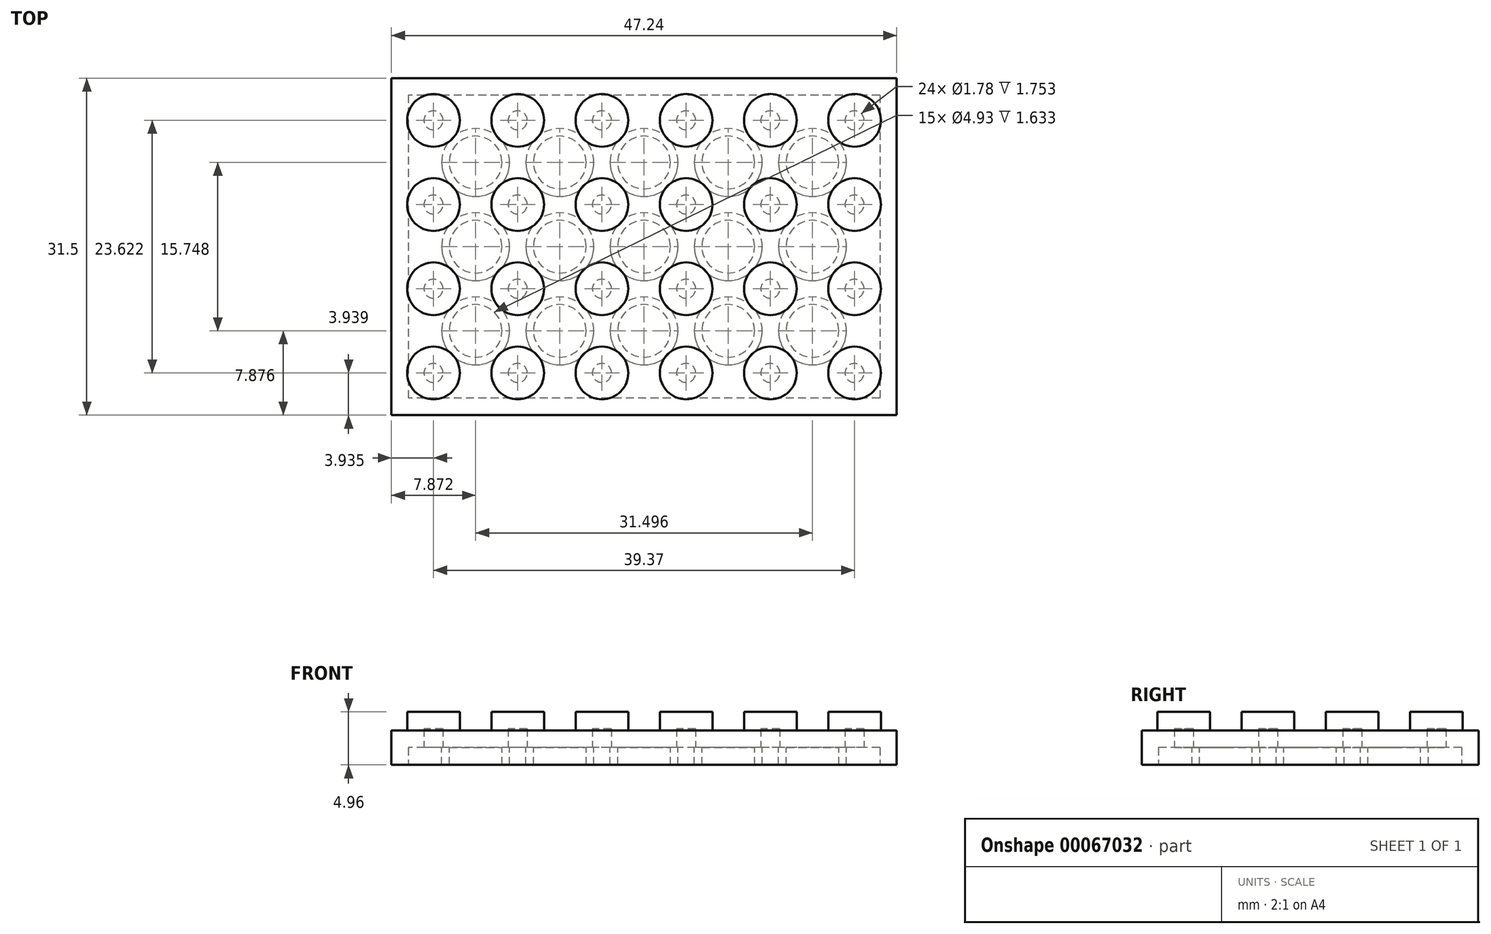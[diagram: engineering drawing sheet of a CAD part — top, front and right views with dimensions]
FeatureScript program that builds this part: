
annotation { "Feature Type Name" : "Feature", "Feature Type Description" : "" }
export const myFeature = defineFeature(function(context is Context, id is Id, definition is map)
    precondition{}
    {
        {
            var Q0;
            Q0=qCreatedBy(makeId("Top.planeOp"),FACE);
            var sketch = newSketch(context, id + "F0", { "sketchPlane" : qUnion([Q0])});
            skLineSegment(sketch, "E0.rect.bottom", {"start": v(23.62, 15.75) * mm, "end": v(-23.62, 15.75) * mm});
            skLineSegment(sketch, "E0.rect.top", {"start": v(23.62, -15.75) * mm, "end": v(-23.62, -15.75) * mm});
            skLineSegment(sketch, "E0.rect.left", {"start": v(23.62, 15.75) * mm, "end": v(23.62, -15.75) * mm});
            skLineSegment(sketch, "E0.rect.right", {"start": v(-23.62, 15.75) * mm, "end": v(-23.62, -15.75) * mm});
            skPoint(sketch, "E0.rect.middle", {"position": v(0, 0) * mm});
            skSolve(sketch);
        }
        {
            var Q0;
            Q0=makeQuery(id+"F0.imprint","IMPRINT",FACE,{"disambiguationData":[TD([[makeQuery(id+"F0.imprint","IMPRINT",EDGE,{"derivedFrom":sQuery(id+"F0.wireOp",EDGE,"E0.rect.bottom")}),1.0]])]});
            extrude(context, id + "F1", {"entities" : qUnion([Q0]), "depth" : 3.2 * mm});
        }
        {
            var Q0;
            Q0=makeQuery(id+"F1.opExtrude","CAP_FACE",FACE,{"disambiguationData":[OSD([sQuery(id+"F0.wireOp",EDGE,"E0.rect.bottom"),sQuery(id+"F0.wireOp",EDGE,"E0.rect.top"),sQuery(id+"F0.wireOp",EDGE,"E0.rect.left"),sQuery(id+"F0.wireOp",EDGE,"E0.rect.right")])],"isStart":false});
            var sketch = newSketch(context, id + "F2", { "sketchPlane" : qUnion([Q0])});
            skLineSegment(sketch, "E1", {"start": v(0, 0) * mm, "end": v(0, 7.87) * mm});
            skLineSegment(sketch, "E2", {"start": v(0, 7.87) * mm, "end": v(0, 15.75) * mm});
            skLineSegment(sketch, "E3", {"start": v(0, 0) * mm, "end": v(0, -7.87) * mm});
            skLineSegment(sketch, "E4", {"start": v(0, -7.87) * mm, "end": v(0, -15.75) * mm});
            skPoint(sketch, "E4.endSnap0", {"position": v(0, -15.75) * mm});
            skLineSegment(sketch, "E5", {"start": v(0, 0) * mm, "end": v(3.94, 0) * mm});
            skLineSegment(sketch, "E6", {"start": v(3.94, 0) * mm, "end": v(11.81, 0) * mm});
            skLineSegment(sketch, "E7", {"start": v(11.81, 0) * mm, "end": v(19.69, 0) * mm});
            skLineSegment(sketch, "E8", {"start": v(0, 0) * mm, "end": v(-3.94, 0) * mm});
            skLineSegment(sketch, "E9", {"start": v(-3.94, 0) * mm, "end": v(-11.81, 0) * mm});
            skLineSegment(sketch, "E10", {"start": v(-11.81, 0) * mm, "end": v(-19.69, 0) * mm});
            skLineSegment(sketch, "E11", {"start": v(-19.69, 0) * mm, "end": v(-19.69, -3.94) * mm});
            skLineSegment(sketch, "E12", {"start": v(-19.69, -3.94) * mm, "end": v(-19.69, -11.81) * mm});
            skLineSegment(sketch, "E13", {"start": v(-19.69, 0) * mm, "end": v(-19.69, 3.94) * mm});
            skLineSegment(sketch, "E14", {"start": v(-19.69, 3.94) * mm, "end": v(-19.69, 11.81) * mm});
            skLineSegment(sketch, "E15", {"start": v(-19.69, 3.94) * mm, "end": v(-11.81, 3.94) * mm});
            skLineSegment(sketch, "E16", {"start": v(-11.81, 3.94) * mm, "end": v(-3.94, 3.94) * mm});
            skLineSegment(sketch, "E17", {"start": v(-3.94, 3.94) * mm, "end": v(-3.94, 11.81) * mm});
            skLineSegment(sketch, "E18", {"start": v(-3.94, 11.81) * mm, "end": v(-11.81, 11.81) * mm});
            skLineSegment(sketch, "E19", {"start": v(-19.69, -3.94) * mm, "end": v(-11.81, -3.94) * mm});
            skLineSegment(sketch, "E20", {"start": v(-11.81, -3.94) * mm, "end": v(-3.94, -3.94) * mm});
            skLineSegment(sketch, "E21", {"start": v(-3.94, -3.94) * mm, "end": v(-3.94, -11.81) * mm});
            skLineSegment(sketch, "E22", {"start": v(-3.94, -11.81) * mm, "end": v(-11.81, -11.81) * mm});
            skLineSegment(sketch, "E23", {"start": v(3.94, 0) * mm, "end": v(3.94, 3.94) * mm});
            skPoint(sketch, "E23.endSnap0", {"position": v(0, 3.94) * mm});
            skLineSegment(sketch, "E24", {"start": v(3.94, 3.94) * mm, "end": v(3.94, 11.81) * mm});
            skPoint(sketch, "E24.endSnap0", {"position": v(0, 11.81) * mm});
            skLineSegment(sketch, "E25", {"start": v(3.94, 11.81) * mm, "end": v(11.81, 11.81) * mm});
            skLineSegment(sketch, "E26", {"start": v(11.81, 11.81) * mm, "end": v(19.69, 11.81) * mm});
            skLineSegment(sketch, "E27", {"start": v(19.69, 11.81) * mm, "end": v(19.69, 3.94) * mm});
            skLineSegment(sketch, "E28", {"start": v(19.69, 3.94) * mm, "end": v(11.81, 3.94) * mm});
            skLineSegment(sketch, "E29", {"start": v(3.94, 0) * mm, "end": v(3.94, -3.94) * mm});
            skPoint(sketch, "E29.endSnap0", {"position": v(0, -3.94) * mm});
            skLineSegment(sketch, "E30", {"start": v(3.94, -3.94) * mm, "end": v(3.94, -11.81) * mm});
            skPoint(sketch, "E30.endSnap0", {"position": v(0, -11.81) * mm});
            skLineSegment(sketch, "E31", {"start": v(3.94, -11.81) * mm, "end": v(11.81, -11.81) * mm});
            skLineSegment(sketch, "E32", {"start": v(11.81, -11.81) * mm, "end": v(19.69, -11.81) * mm});
            skLineSegment(sketch, "E33", {"start": v(19.69, -11.81) * mm, "end": v(19.69, -3.94) * mm});
            skLineSegment(sketch, "E34", {"start": v(19.69, -3.94) * mm, "end": v(11.81, -3.94) * mm});
            skCircle(sketch, "E35", {"center": v(-19.69, 11.81) * mm, "radius": 2.46 * mm});
            skCircle(sketch, "E36", {"center": v(-11.81, 11.81) * mm, "radius": 2.46 * mm});
            skCircle(sketch, "E37", {"center": v(-3.94, 11.81) * mm, "radius": 2.46 * mm});
            skCircle(sketch, "E38", {"center": v(3.94, 11.81) * mm, "radius": 2.46 * mm});
            skCircle(sketch, "E39", {"center": v(11.81, 11.81) * mm, "radius": 2.46 * mm});
            skCircle(sketch, "E40", {"center": v(19.69, 11.81) * mm, "radius": 2.46 * mm});
            skCircle(sketch, "E41", {"center": v(19.69, 3.94) * mm, "radius": 2.46 * mm});
            skCircle(sketch, "E42", {"center": v(11.81, 3.94) * mm, "radius": 2.46 * mm});
            skCircle(sketch, "E43", {"center": v(3.94, 3.94) * mm, "radius": 2.46 * mm});
            skCircle(sketch, "E44", {"center": v(-3.94, 3.94) * mm, "radius": 2.46 * mm});
            skCircle(sketch, "E45", {"center": v(-11.81, 3.94) * mm, "radius": 2.46 * mm});
            skCircle(sketch, "E46", {"center": v(-19.69, 3.94) * mm, "radius": 2.46 * mm});
            skCircle(sketch, "E47", {"center": v(-19.69, -3.94) * mm, "radius": 2.46 * mm});
            skCircle(sketch, "E48", {"center": v(-11.81, -3.94) * mm, "radius": 2.46 * mm});
            skCircle(sketch, "E49", {"center": v(-3.94, -3.94) * mm, "radius": 2.46 * mm});
            skCircle(sketch, "E50", {"center": v(-3.94, -11.81) * mm, "radius": 2.46 * mm});
            skCircle(sketch, "E51", {"center": v(-11.81, -11.81) * mm, "radius": 2.46 * mm});
            skCircle(sketch, "E52", {"center": v(-19.69, -11.81) * mm, "radius": 2.46 * mm});
            skCircle(sketch, "E53", {"center": v(3.94, -11.81) * mm, "radius": 2.46 * mm});
            skCircle(sketch, "E54", {"center": v(11.81, -11.81) * mm, "radius": 2.46 * mm});
            skCircle(sketch, "E55", {"center": v(19.69, -11.81) * mm, "radius": 2.46 * mm});
            skCircle(sketch, "E56", {"center": v(19.69, -3.94) * mm, "radius": 2.46 * mm});
            skCircle(sketch, "E57", {"center": v(11.81, -3.94) * mm, "radius": 2.46 * mm});
            skCircle(sketch, "E58", {"center": v(3.94, -3.94) * mm, "radius": 2.46 * mm});
            skSolve(sketch);
        }
        {
            var Q0;
            Q0=makeQuery(id+"F2.imprint","IMPRINT",FACE,{"disambiguationData":[TD([[makeQuery(id+"F2.imprint","IMPRINT",EDGE,{"derivedFrom":sQuery(id+"F2.wireOp",EDGE,"E35")}),1.0]])]});
            var Q1;
            Q1=makeQuery(id+"F2.imprint","IMPRINT",FACE,{"disambiguationData":[TD([[makeQuery(id+"F2.imprint","IMPRINT",EDGE,{"derivedFrom":sQuery(id+"F2.wireOp",EDGE,"E36")}),1.0]])]});
            var Q2;
            {var subQ0=sQuery(id+"F2.wireOp",EDGE,"E18");var subQ1=sQuery(id+"F2.wireOp",EDGE,"E17");var subQ2=makeQuery(id+"F2.imprint","INTERSECT",VERTEX,{"derivedFrom":[subQ1,subQ0]});Q2=makeQuery(id+"F2.imprint","IMPRINT",FACE,{"disambiguationData":[TD([[makeQuery(id+"F2.imprint","IMPRINT",EDGE,{"disambiguationData":[TD([[subQ2,1.0]])],"derivedFrom":subQ1}),-1.0]])]});}
            var Q3;
            {var subQ0=sQuery(id+"F2.wireOp",EDGE,"E18");var subQ1=sQuery(id+"F2.wireOp",EDGE,"E17");var subQ2=makeQuery(id+"F2.imprint","INTERSECT",VERTEX,{"derivedFrom":[subQ1,subQ0]});Q3=makeQuery(id+"F2.imprint","IMPRINT",FACE,{"disambiguationData":[TD([[makeQuery(id+"F2.imprint","IMPRINT",EDGE,{"disambiguationData":[TD([[subQ2,1.0]])],"derivedFrom":subQ1}),1.0]])]});}
            var Q4;
            {var subQ0=sQuery(id+"F2.wireOp",EDGE,"E25");var subQ1=sQuery(id+"F2.wireOp",EDGE,"E24");var subQ2=makeQuery(id+"F2.imprint","INTERSECT",VERTEX,{"derivedFrom":[subQ1,subQ0]});Q4=makeQuery(id+"F2.imprint","IMPRINT",FACE,{"disambiguationData":[TD([[makeQuery(id+"F2.imprint","IMPRINT",EDGE,{"disambiguationData":[TD([[subQ2,1.0]])],"derivedFrom":subQ1}),1.0]])]});}
            var Q5;
            {var subQ0=sQuery(id+"F2.wireOp",EDGE,"E25");var subQ1=sQuery(id+"F2.wireOp",EDGE,"E24");var subQ2=makeQuery(id+"F2.imprint","INTERSECT",VERTEX,{"derivedFrom":[subQ1,subQ0]});Q5=makeQuery(id+"F2.imprint","IMPRINT",FACE,{"disambiguationData":[TD([[makeQuery(id+"F2.imprint","IMPRINT",EDGE,{"disambiguationData":[TD([[subQ2,1.0]])],"derivedFrom":subQ1}),-1.0]])]});}
            var Q6;
            {var subQ0=sQuery(id+"F2.wireOp",EDGE,"E24");var subQ1=sQuery(id+"F2.wireOp",EDGE,"E23");var subQ2=makeQuery(id+"F2.imprint","INTERSECT",VERTEX,{"derivedFrom":[subQ1,subQ0]});Q6=makeQuery(id+"F2.imprint","IMPRINT",FACE,{"disambiguationData":[TD([[makeQuery(id+"F2.imprint","IMPRINT",EDGE,{"disambiguationData":[TD([[subQ2,1.0]])],"derivedFrom":subQ1}),-1.0]])]});}
            var Q7;
            {var subQ0=sQuery(id+"F2.wireOp",EDGE,"E24");var subQ1=sQuery(id+"F2.wireOp",EDGE,"E23");var subQ2=makeQuery(id+"F2.imprint","INTERSECT",VERTEX,{"derivedFrom":[subQ1,subQ0]});Q7=makeQuery(id+"F2.imprint","IMPRINT",FACE,{"disambiguationData":[TD([[makeQuery(id+"F2.imprint","IMPRINT",EDGE,{"disambiguationData":[TD([[subQ2,1.0]])],"derivedFrom":subQ1}),1.0]])]});}
            var Q8;
            {var subQ0=sQuery(id+"F2.wireOp",EDGE,"E17");var subQ1=sQuery(id+"F2.wireOp",EDGE,"E16");var subQ2=makeQuery(id+"F2.imprint","INTERSECT",VERTEX,{"derivedFrom":[subQ1,subQ0]});Q8=makeQuery(id+"F2.imprint","IMPRINT",FACE,{"disambiguationData":[TD([[makeQuery(id+"F2.imprint","IMPRINT",EDGE,{"disambiguationData":[TD([[subQ2,1.0]])],"derivedFrom":subQ1}),-1.0]])]});}
            var Q9;
            {var subQ0=sQuery(id+"F2.wireOp",EDGE,"E17");var subQ1=sQuery(id+"F2.wireOp",EDGE,"E16");var subQ2=makeQuery(id+"F2.imprint","INTERSECT",VERTEX,{"derivedFrom":[subQ1,subQ0]});Q9=makeQuery(id+"F2.imprint","IMPRINT",FACE,{"disambiguationData":[TD([[makeQuery(id+"F2.imprint","IMPRINT",EDGE,{"disambiguationData":[TD([[subQ2,1.0]])],"derivedFrom":subQ1}),1.0]])]});}
            var Q10;
            {var subQ0=sQuery(id+"F2.wireOp",EDGE,"E16");var subQ1=sQuery(id+"F2.wireOp",EDGE,"E15");var subQ2=makeQuery(id+"F2.imprint","INTERSECT",VERTEX,{"derivedFrom":[subQ1,subQ0]});Q10=makeQuery(id+"F2.imprint","IMPRINT",FACE,{"disambiguationData":[TD([[makeQuery(id+"F2.imprint","IMPRINT",EDGE,{"disambiguationData":[TD([[subQ2,1.0]])],"derivedFrom":subQ1}),1.0]])]});}
            var Q11;
            {var subQ0=sQuery(id+"F2.wireOp",EDGE,"E16");var subQ1=sQuery(id+"F2.wireOp",EDGE,"E15");var subQ2=makeQuery(id+"F2.imprint","INTERSECT",VERTEX,{"derivedFrom":[subQ1,subQ0]});Q11=makeQuery(id+"F2.imprint","IMPRINT",FACE,{"disambiguationData":[TD([[makeQuery(id+"F2.imprint","IMPRINT",EDGE,{"disambiguationData":[TD([[subQ2,1.0]])],"derivedFrom":subQ1}),-1.0]])]});}
            var Q12;
            {var subQ1=sQuery(id+"F2.wireOp",EDGE,"E14");var subQ3=sQuery(id+"F2.wireOp",EDGE,"E46");var subQ4=makeQuery(id+"F2.imprint","INTERSECT",VERTEX,{"derivedFrom":[subQ1,subQ3]});Q12=makeQuery(id+"F2.imprint","IMPRINT",FACE,{"disambiguationData":[TD([[makeQuery(id+"F2.imprint","IMPRINT",EDGE,{"disambiguationData":[TD([[subQ4,1.0]])],"derivedFrom":subQ3}),1.0]])]});}
            var Q13;
            {var subQ1=sQuery(id+"F2.wireOp",EDGE,"E13");var subQ3=sQuery(id+"F2.wireOp",EDGE,"E46");var subQ4=makeQuery(id+"F2.imprint","INTERSECT",VERTEX,{"derivedFrom":[subQ1,subQ3]});Q13=makeQuery(id+"F2.imprint","IMPRINT",FACE,{"disambiguationData":[TD([[makeQuery(id+"F2.imprint","IMPRINT",EDGE,{"disambiguationData":[TD([[subQ4,-1.0]])],"derivedFrom":subQ3}),1.0]])]});}
            var Q14;
            {var subQ1=sQuery(id+"F2.wireOp",EDGE,"E13");var subQ3=sQuery(id+"F2.wireOp",EDGE,"E46");var subQ4=makeQuery(id+"F2.imprint","INTERSECT",VERTEX,{"derivedFrom":[subQ1,subQ3]});Q14=makeQuery(id+"F2.imprint","IMPRINT",FACE,{"disambiguationData":[TD([[makeQuery(id+"F2.imprint","IMPRINT",EDGE,{"disambiguationData":[TD([[subQ4,1.0]])],"derivedFrom":subQ3}),1.0]])]});}
            var Q15;
            {var subQ1=sQuery(id+"F2.wireOp",EDGE,"E11");var subQ3=sQuery(id+"F2.wireOp",EDGE,"E47");var subQ4=makeQuery(id+"F2.imprint","INTERSECT",VERTEX,{"derivedFrom":[subQ1,subQ3]});Q15=makeQuery(id+"F2.imprint","IMPRINT",FACE,{"disambiguationData":[TD([[makeQuery(id+"F2.imprint","IMPRINT",EDGE,{"disambiguationData":[TD([[subQ4,1.0]])],"derivedFrom":subQ3}),1.0]])]});}
            var Q16;
            {var subQ1=sQuery(id+"F2.wireOp",EDGE,"E12");var subQ3=sQuery(id+"F2.wireOp",EDGE,"E47");var subQ4=makeQuery(id+"F2.imprint","INTERSECT",VERTEX,{"derivedFrom":[subQ1,subQ3]});Q16=makeQuery(id+"F2.imprint","IMPRINT",FACE,{"disambiguationData":[TD([[makeQuery(id+"F2.imprint","IMPRINT",EDGE,{"disambiguationData":[TD([[subQ4,-1.0]])],"derivedFrom":subQ3}),1.0]])]});}
            var Q17;
            {var subQ1=sQuery(id+"F2.wireOp",EDGE,"E11");var subQ3=sQuery(id+"F2.wireOp",EDGE,"E47");var subQ4=makeQuery(id+"F2.imprint","INTERSECT",VERTEX,{"derivedFrom":[subQ1,subQ3]});Q17=makeQuery(id+"F2.imprint","IMPRINT",FACE,{"disambiguationData":[TD([[makeQuery(id+"F2.imprint","IMPRINT",EDGE,{"disambiguationData":[TD([[subQ4,-1.0]])],"derivedFrom":subQ3}),1.0]])]});}
            var Q18;
            {var subQ0=sQuery(id+"F2.wireOp",EDGE,"E20");var subQ1=sQuery(id+"F2.wireOp",EDGE,"E19");var subQ2=makeQuery(id+"F2.imprint","INTERSECT",VERTEX,{"derivedFrom":[subQ1,subQ0]});Q18=makeQuery(id+"F2.imprint","IMPRINT",FACE,{"disambiguationData":[TD([[makeQuery(id+"F2.imprint","IMPRINT",EDGE,{"disambiguationData":[TD([[subQ2,1.0]])],"derivedFrom":subQ1}),1.0]])]});}
            var Q19;
            {var subQ0=sQuery(id+"F2.wireOp",EDGE,"E20");var subQ1=sQuery(id+"F2.wireOp",EDGE,"E19");var subQ2=makeQuery(id+"F2.imprint","INTERSECT",VERTEX,{"derivedFrom":[subQ1,subQ0]});Q19=makeQuery(id+"F2.imprint","IMPRINT",FACE,{"disambiguationData":[TD([[makeQuery(id+"F2.imprint","IMPRINT",EDGE,{"disambiguationData":[TD([[subQ2,1.0]])],"derivedFrom":subQ1}),-1.0]])]});}
            var Q20;
            {var subQ0=sQuery(id+"F2.wireOp",EDGE,"E21");var subQ1=sQuery(id+"F2.wireOp",EDGE,"E20");var subQ2=makeQuery(id+"F2.imprint","INTERSECT",VERTEX,{"derivedFrom":[subQ1,subQ0]});Q20=makeQuery(id+"F2.imprint","IMPRINT",FACE,{"disambiguationData":[TD([[makeQuery(id+"F2.imprint","IMPRINT",EDGE,{"disambiguationData":[TD([[subQ2,1.0]])],"derivedFrom":subQ1}),-1.0]])]});}
            var Q21;
            {var subQ0=sQuery(id+"F2.wireOp",EDGE,"E21");var subQ1=sQuery(id+"F2.wireOp",EDGE,"E20");var subQ2=makeQuery(id+"F2.imprint","INTERSECT",VERTEX,{"derivedFrom":[subQ1,subQ0]});Q21=makeQuery(id+"F2.imprint","IMPRINT",FACE,{"disambiguationData":[TD([[makeQuery(id+"F2.imprint","IMPRINT",EDGE,{"disambiguationData":[TD([[subQ2,1.0]])],"derivedFrom":subQ1}),1.0]])]});}
            var Q22;
            {var subQ0=sQuery(id+"F2.wireOp",EDGE,"E22");var subQ1=sQuery(id+"F2.wireOp",EDGE,"E21");var subQ2=makeQuery(id+"F2.imprint","INTERSECT",VERTEX,{"derivedFrom":[subQ1,subQ0]});Q22=makeQuery(id+"F2.imprint","IMPRINT",FACE,{"disambiguationData":[TD([[makeQuery(id+"F2.imprint","IMPRINT",EDGE,{"disambiguationData":[TD([[subQ2,1.0]])],"derivedFrom":subQ1}),1.0]])]});}
            var Q23;
            {var subQ0=sQuery(id+"F2.wireOp",EDGE,"E22");var subQ1=sQuery(id+"F2.wireOp",EDGE,"E21");var subQ2=makeQuery(id+"F2.imprint","INTERSECT",VERTEX,{"derivedFrom":[subQ1,subQ0]});Q23=makeQuery(id+"F2.imprint","IMPRINT",FACE,{"disambiguationData":[TD([[makeQuery(id+"F2.imprint","IMPRINT",EDGE,{"disambiguationData":[TD([[subQ2,1.0]])],"derivedFrom":subQ1}),-1.0]])]});}
            var Q24;
            Q24=makeQuery(id+"F2.imprint","IMPRINT",FACE,{"disambiguationData":[TD([[makeQuery(id+"F2.imprint","IMPRINT",EDGE,{"derivedFrom":sQuery(id+"F2.wireOp",EDGE,"E51")}),1.0]])]});
            var Q25;
            Q25=makeQuery(id+"F2.imprint","IMPRINT",FACE,{"disambiguationData":[TD([[makeQuery(id+"F2.imprint","IMPRINT",EDGE,{"derivedFrom":sQuery(id+"F2.wireOp",EDGE,"E52")}),1.0]])]});
            var Q26;
            {var subQ0=sQuery(id+"F2.wireOp",EDGE,"E31");var subQ1=sQuery(id+"F2.wireOp",EDGE,"E30");var subQ2=makeQuery(id+"F2.imprint","INTERSECT",VERTEX,{"derivedFrom":[subQ1,subQ0]});Q26=makeQuery(id+"F2.imprint","IMPRINT",FACE,{"disambiguationData":[TD([[makeQuery(id+"F2.imprint","IMPRINT",EDGE,{"disambiguationData":[TD([[subQ2,1.0]])],"derivedFrom":subQ1}),-1.0]])]});}
            var Q27;
            {var subQ0=sQuery(id+"F2.wireOp",EDGE,"E31");var subQ1=sQuery(id+"F2.wireOp",EDGE,"E30");var subQ2=makeQuery(id+"F2.imprint","INTERSECT",VERTEX,{"derivedFrom":[subQ1,subQ0]});Q27=makeQuery(id+"F2.imprint","IMPRINT",FACE,{"disambiguationData":[TD([[makeQuery(id+"F2.imprint","IMPRINT",EDGE,{"disambiguationData":[TD([[subQ2,1.0]])],"derivedFrom":subQ1}),1.0]])]});}
            var Q28;
            {var subQ0=sQuery(id+"F2.wireOp",EDGE,"E30");var subQ1=sQuery(id+"F2.wireOp",EDGE,"E29");var subQ2=makeQuery(id+"F2.imprint","INTERSECT",VERTEX,{"derivedFrom":[subQ1,subQ0]});Q28=makeQuery(id+"F2.imprint","IMPRINT",FACE,{"disambiguationData":[TD([[makeQuery(id+"F2.imprint","IMPRINT",EDGE,{"disambiguationData":[TD([[subQ2,1.0]])],"derivedFrom":subQ1}),1.0]])]});}
            var Q29;
            {var subQ0=sQuery(id+"F2.wireOp",EDGE,"E30");var subQ1=sQuery(id+"F2.wireOp",EDGE,"E29");var subQ2=makeQuery(id+"F2.imprint","INTERSECT",VERTEX,{"derivedFrom":[subQ1,subQ0]});Q29=makeQuery(id+"F2.imprint","IMPRINT",FACE,{"disambiguationData":[TD([[makeQuery(id+"F2.imprint","IMPRINT",EDGE,{"disambiguationData":[TD([[subQ2,1.0]])],"derivedFrom":subQ1}),-1.0]])]});}
            var Q30;
            Q30=makeQuery(id+"F2.imprint","IMPRINT",FACE,{"disambiguationData":[TD([[makeQuery(id+"F2.imprint","IMPRINT",EDGE,{"derivedFrom":sQuery(id+"F2.wireOp",EDGE,"E57")}),1.0]])]});
            var Q31;
            {var subQ0=sQuery(id+"F2.wireOp",EDGE,"E34");var subQ1=sQuery(id+"F2.wireOp",EDGE,"E33");var subQ2=makeQuery(id+"F2.imprint","INTERSECT",VERTEX,{"derivedFrom":[subQ1,subQ0]});Q31=makeQuery(id+"F2.imprint","IMPRINT",FACE,{"disambiguationData":[TD([[makeQuery(id+"F2.imprint","IMPRINT",EDGE,{"disambiguationData":[TD([[subQ2,1.0]])],"derivedFrom":subQ1}),-1.0]])]});}
            var Q32;
            {var subQ0=sQuery(id+"F2.wireOp",EDGE,"E34");var subQ1=sQuery(id+"F2.wireOp",EDGE,"E33");var subQ2=makeQuery(id+"F2.imprint","INTERSECT",VERTEX,{"derivedFrom":[subQ1,subQ0]});Q32=makeQuery(id+"F2.imprint","IMPRINT",FACE,{"disambiguationData":[TD([[makeQuery(id+"F2.imprint","IMPRINT",EDGE,{"disambiguationData":[TD([[subQ2,1.0]])],"derivedFrom":subQ1}),1.0]])]});}
            var Q33;
            {var subQ0=sQuery(id+"F2.wireOp",EDGE,"E33");var subQ1=sQuery(id+"F2.wireOp",EDGE,"E32");var subQ2=makeQuery(id+"F2.imprint","INTERSECT",VERTEX,{"derivedFrom":[subQ1,subQ0]});Q33=makeQuery(id+"F2.imprint","IMPRINT",FACE,{"disambiguationData":[TD([[makeQuery(id+"F2.imprint","IMPRINT",EDGE,{"disambiguationData":[TD([[subQ2,1.0]])],"derivedFrom":subQ1}),-1.0]])]});}
            var Q34;
            {var subQ0=sQuery(id+"F2.wireOp",EDGE,"E33");var subQ1=sQuery(id+"F2.wireOp",EDGE,"E32");var subQ2=makeQuery(id+"F2.imprint","INTERSECT",VERTEX,{"derivedFrom":[subQ1,subQ0]});Q34=makeQuery(id+"F2.imprint","IMPRINT",FACE,{"disambiguationData":[TD([[makeQuery(id+"F2.imprint","IMPRINT",EDGE,{"disambiguationData":[TD([[subQ2,1.0]])],"derivedFrom":subQ1}),1.0]])]});}
            var Q35;
            {var subQ0=sQuery(id+"F2.wireOp",EDGE,"E32");var subQ1=sQuery(id+"F2.wireOp",EDGE,"E31");var subQ2=makeQuery(id+"F2.imprint","INTERSECT",VERTEX,{"derivedFrom":[subQ1,subQ0]});Q35=makeQuery(id+"F2.imprint","IMPRINT",FACE,{"disambiguationData":[TD([[makeQuery(id+"F2.imprint","IMPRINT",EDGE,{"disambiguationData":[TD([[subQ2,1.0]])],"derivedFrom":subQ1}),1.0]])]});}
            var Q36;
            {var subQ0=sQuery(id+"F2.wireOp",EDGE,"E32");var subQ1=sQuery(id+"F2.wireOp",EDGE,"E31");var subQ2=makeQuery(id+"F2.imprint","INTERSECT",VERTEX,{"derivedFrom":[subQ1,subQ0]});Q36=makeQuery(id+"F2.imprint","IMPRINT",FACE,{"disambiguationData":[TD([[makeQuery(id+"F2.imprint","IMPRINT",EDGE,{"disambiguationData":[TD([[subQ2,1.0]])],"derivedFrom":subQ1}),-1.0]])]});}
            var Q37;
            {var subQ0=sQuery(id+"F2.wireOp",EDGE,"E28");var subQ1=sQuery(id+"F2.wireOp",EDGE,"E27");var subQ2=makeQuery(id+"F2.imprint","INTERSECT",VERTEX,{"derivedFrom":[subQ1,subQ0]});Q37=makeQuery(id+"F2.imprint","IMPRINT",FACE,{"disambiguationData":[TD([[makeQuery(id+"F2.imprint","IMPRINT",EDGE,{"disambiguationData":[TD([[subQ2,1.0]])],"derivedFrom":subQ1}),1.0]])]});}
            var Q38;
            {var subQ0=sQuery(id+"F2.wireOp",EDGE,"E28");var subQ1=sQuery(id+"F2.wireOp",EDGE,"E27");var subQ2=makeQuery(id+"F2.imprint","INTERSECT",VERTEX,{"derivedFrom":[subQ1,subQ0]});Q38=makeQuery(id+"F2.imprint","IMPRINT",FACE,{"disambiguationData":[TD([[makeQuery(id+"F2.imprint","IMPRINT",EDGE,{"disambiguationData":[TD([[subQ2,1.0]])],"derivedFrom":subQ1}),-1.0]])]});}
            var Q39;
            Q39=makeQuery(id+"F2.imprint","IMPRINT",FACE,{"disambiguationData":[TD([[makeQuery(id+"F2.imprint","IMPRINT",EDGE,{"derivedFrom":sQuery(id+"F2.wireOp",EDGE,"E42")}),1.0]])]});
            var Q40;
            {var subQ0=sQuery(id+"F2.wireOp",EDGE,"E26");var subQ1=sQuery(id+"F2.wireOp",EDGE,"E25");var subQ2=makeQuery(id+"F2.imprint","INTERSECT",VERTEX,{"derivedFrom":[subQ1,subQ0]});Q40=makeQuery(id+"F2.imprint","IMPRINT",FACE,{"disambiguationData":[TD([[makeQuery(id+"F2.imprint","IMPRINT",EDGE,{"disambiguationData":[TD([[subQ2,1.0]])],"derivedFrom":subQ1}),-1.0]])]});}
            var Q41;
            {var subQ0=sQuery(id+"F2.wireOp",EDGE,"E26");var subQ1=sQuery(id+"F2.wireOp",EDGE,"E25");var subQ2=makeQuery(id+"F2.imprint","INTERSECT",VERTEX,{"derivedFrom":[subQ1,subQ0]});Q41=makeQuery(id+"F2.imprint","IMPRINT",FACE,{"disambiguationData":[TD([[makeQuery(id+"F2.imprint","IMPRINT",EDGE,{"disambiguationData":[TD([[subQ2,1.0]])],"derivedFrom":subQ1}),1.0]])]});}
            var Q42;
            {var subQ0=sQuery(id+"F2.wireOp",EDGE,"E27");var subQ1=sQuery(id+"F2.wireOp",EDGE,"E26");var subQ2=makeQuery(id+"F2.imprint","INTERSECT",VERTEX,{"derivedFrom":[subQ1,subQ0]});Q42=makeQuery(id+"F2.imprint","IMPRINT",FACE,{"disambiguationData":[TD([[makeQuery(id+"F2.imprint","IMPRINT",EDGE,{"disambiguationData":[TD([[subQ2,1.0]])],"derivedFrom":subQ1}),1.0]])]});}
            var Q43;
            {var subQ0=sQuery(id+"F2.wireOp",EDGE,"E27");var subQ1=sQuery(id+"F2.wireOp",EDGE,"E26");var subQ2=makeQuery(id+"F2.imprint","INTERSECT",VERTEX,{"derivedFrom":[subQ1,subQ0]});Q43=makeQuery(id+"F2.imprint","IMPRINT",FACE,{"disambiguationData":[TD([[makeQuery(id+"F2.imprint","IMPRINT",EDGE,{"disambiguationData":[TD([[subQ2,1.0]])],"derivedFrom":subQ1}),-1.0]])]});}
            extrude(context, id + "F3", {"entities" : qUnion([Q0, Q1, Q2, Q3, Q4, Q5, Q6, Q7, Q8, Q9, Q10, Q11, Q12, Q13, Q14, Q15, Q16, Q17, Q18, Q19, Q20, Q21, Q22, Q23, Q24, Q25, Q26, Q27, Q28, Q29, Q30, Q31, Q32, Q33, Q34, Q35, Q36, Q37, Q38, Q39, Q40, Q41, Q42, Q43]), "operationType" : NewBodyOperationType.ADD, "depth" : 1.75 * mm});
        }
        {
            var Q0;
            Q0=makeQuery(id+"F1.opExtrude","CAP_FACE",FACE,{"disambiguationData":[OSD([sQuery(id+"F0.wireOp",EDGE,"E0.rect.bottom"),sQuery(id+"F0.wireOp",EDGE,"E0.rect.top"),sQuery(id+"F0.wireOp",EDGE,"E0.rect.left"),sQuery(id+"F0.wireOp",EDGE,"E0.rect.right")])],"isStart":true});
            shell(context, id + "F4", {"entities" : qUnion([Q0]), "thickness" : 1.57 * mm});
        }
        {
            var Q0;
            Q0=makeQuery(id+"F4.opShell","OFFSET_FACE",FACE,{"disambiguationData":[OSD([sQuery(id+"F0.wireOp",EDGE,"E0.rect.bottom"),sQuery(id+"F0.wireOp",EDGE,"E0.rect.top"),sQuery(id+"F0.wireOp",EDGE,"E0.rect.left"),sQuery(id+"F0.wireOp",EDGE,"E0.rect.right")])]});
            var sketch = newSketch(context, id + "F5", { "sketchPlane" : qUnion([Q0])});
            skCircle(sketch, "E59", {"center": v(-7.87, 7.87) * mm, "radius": 2.46 * mm});
            skCircle(sketch, "E60", {"center": v(-15.75, 7.87) * mm, "radius": 2.46 * mm});
            skCircle(sketch, "E61", {"center": v(0, 7.87) * mm, "radius": 2.46 * mm});
            skCircle(sketch, "E62", {"center": v(7.87, 7.87) * mm, "radius": 2.46 * mm});
            skCircle(sketch, "E63", {"center": v(15.75, 7.87) * mm, "radius": 2.46 * mm});
            skCircle(sketch, "E64", {"center": v(15.75, 0) * mm, "radius": 2.46 * mm});
            skCircle(sketch, "E65", {"center": v(7.87, 0) * mm, "radius": 2.46 * mm});
            skCircle(sketch, "E66", {"center": v(0, 0) * mm, "radius": 2.46 * mm});
            skCircle(sketch, "E67", {"center": v(-7.87, 0) * mm, "radius": 2.46 * mm});
            skCircle(sketch, "E68", {"center": v(-15.75, 0) * mm, "radius": 2.46 * mm});
            skCircle(sketch, "E69", {"center": v(-15.75, -7.87) * mm, "radius": 2.46 * mm});
            skCircle(sketch, "E70", {"center": v(-7.87, -7.87) * mm, "radius": 2.46 * mm});
            skCircle(sketch, "E71", {"center": v(0, -7.87) * mm, "radius": 2.46 * mm});
            skCircle(sketch, "E72", {"center": v(7.87, -7.87) * mm, "radius": 2.46 * mm});
            skCircle(sketch, "E73", {"center": v(15.75, -7.87) * mm, "radius": 2.46 * mm});
            skCircle(sketch, "E74", {"center": v(-15.75, 7.87) * mm, "radius": 3.18 * mm});
            skCircle(sketch, "E75", {"center": v(-7.87, 7.87) * mm, "radius": 3.18 * mm});
            skCircle(sketch, "E76", {"center": v(0, 7.87) * mm, "radius": 3.18 * mm});
            skCircle(sketch, "E77", {"center": v(7.87, 7.87) * mm, "radius": 3.18 * mm});
            skCircle(sketch, "E78", {"center": v(15.75, 7.87) * mm, "radius": 3.18 * mm});
            skCircle(sketch, "E79", {"center": v(15.75, 0) * mm, "radius": 3.18 * mm});
            skCircle(sketch, "E80", {"center": v(7.87, 0) * mm, "radius": 3.18 * mm});
            skCircle(sketch, "E81", {"center": v(0, 0) * mm, "radius": 3.18 * mm});
            skCircle(sketch, "E82", {"center": v(-7.87, 0) * mm, "radius": 3.18 * mm});
            skCircle(sketch, "E83", {"center": v(-15.75, 0) * mm, "radius": 3.18 * mm});
            skCircle(sketch, "E84", {"center": v(-15.75, -7.87) * mm, "radius": 3.18 * mm});
            skCircle(sketch, "E85", {"center": v(-7.87, -7.87) * mm, "radius": 3.18 * mm});
            skCircle(sketch, "E86", {"center": v(0, -7.87) * mm, "radius": 3.18 * mm});
            skCircle(sketch, "E87", {"center": v(7.87, -7.87) * mm, "radius": 3.18 * mm});
            skCircle(sketch, "E88", {"center": v(15.75, -7.87) * mm, "radius": 3.18 * mm});
            skSolve(sketch);
        }
        {
            var Q0;
            Q0=makeQuery(id+"F5.imprint","IMPRINT",FACE,{"disambiguationData":[TD([[makeQuery(id+"F5.imprint","IMPRINT",EDGE,{"derivedFrom":sQuery(id+"F5.wireOp",EDGE,"E60")}),-1.0]])]});
            var Q1;
            Q1=makeQuery(id+"F5.imprint","IMPRINT",FACE,{"disambiguationData":[TD([[makeQuery(id+"F5.imprint","IMPRINT",EDGE,{"derivedFrom":sQuery(id+"F5.wireOp",EDGE,"E59")}),-1.0]])]});
            var Q2;
            Q2=makeQuery(id+"F5.imprint","IMPRINT",FACE,{"disambiguationData":[TD([[makeQuery(id+"F5.imprint","IMPRINT",EDGE,{"derivedFrom":sQuery(id+"F5.wireOp",EDGE,"E61")}),-1.0]])]});
            var Q3;
            Q3=makeQuery(id+"F5.imprint","IMPRINT",FACE,{"disambiguationData":[TD([[makeQuery(id+"F5.imprint","IMPRINT",EDGE,{"derivedFrom":sQuery(id+"F5.wireOp",EDGE,"E62")}),-1.0]])]});
            var Q4;
            Q4=makeQuery(id+"F5.imprint","IMPRINT",FACE,{"disambiguationData":[TD([[makeQuery(id+"F5.imprint","IMPRINT",EDGE,{"derivedFrom":sQuery(id+"F5.wireOp",EDGE,"E63")}),-1.0]])]});
            var Q5;
            Q5=makeQuery(id+"F5.imprint","IMPRINT",FACE,{"disambiguationData":[TD([[makeQuery(id+"F5.imprint","IMPRINT",EDGE,{"derivedFrom":sQuery(id+"F5.wireOp",EDGE,"E64")}),-1.0]])]});
            var Q6;
            Q6=makeQuery(id+"F5.imprint","IMPRINT",FACE,{"disambiguationData":[TD([[makeQuery(id+"F5.imprint","IMPRINT",EDGE,{"derivedFrom":sQuery(id+"F5.wireOp",EDGE,"E65")}),-1.0]])]});
            var Q7;
            Q7=makeQuery(id+"F5.imprint","IMPRINT",FACE,{"disambiguationData":[TD([[makeQuery(id+"F5.imprint","IMPRINT",EDGE,{"derivedFrom":sQuery(id+"F5.wireOp",EDGE,"E66")}),-1.0]])]});
            var Q8;
            Q8=makeQuery(id+"F5.imprint","IMPRINT",FACE,{"disambiguationData":[TD([[makeQuery(id+"F5.imprint","IMPRINT",EDGE,{"derivedFrom":sQuery(id+"F5.wireOp",EDGE,"E67")}),-1.0]])]});
            var Q9;
            Q9=makeQuery(id+"F5.imprint","IMPRINT",FACE,{"disambiguationData":[TD([[makeQuery(id+"F5.imprint","IMPRINT",EDGE,{"derivedFrom":sQuery(id+"F5.wireOp",EDGE,"E68")}),-1.0]])]});
            var Q10;
            Q10=makeQuery(id+"F5.imprint","IMPRINT",FACE,{"disambiguationData":[TD([[makeQuery(id+"F5.imprint","IMPRINT",EDGE,{"derivedFrom":sQuery(id+"F5.wireOp",EDGE,"E69")}),-1.0]])]});
            var Q11;
            Q11=makeQuery(id+"F5.imprint","IMPRINT",FACE,{"disambiguationData":[TD([[makeQuery(id+"F5.imprint","IMPRINT",EDGE,{"derivedFrom":sQuery(id+"F5.wireOp",EDGE,"E70")}),-1.0]])]});
            var Q12;
            Q12=makeQuery(id+"F5.imprint","IMPRINT",FACE,{"disambiguationData":[TD([[makeQuery(id+"F5.imprint","IMPRINT",EDGE,{"derivedFrom":sQuery(id+"F5.wireOp",EDGE,"E71")}),-1.0]])]});
            var Q13;
            Q13=makeQuery(id+"F5.imprint","IMPRINT",FACE,{"disambiguationData":[TD([[makeQuery(id+"F5.imprint","IMPRINT",EDGE,{"derivedFrom":sQuery(id+"F5.wireOp",EDGE,"E72")}),-1.0]])]});
            var Q14;
            Q14=makeQuery(id+"F5.imprint","IMPRINT",FACE,{"disambiguationData":[TD([[makeQuery(id+"F5.imprint","IMPRINT",EDGE,{"derivedFrom":sQuery(id+"F5.wireOp",EDGE,"E73")}),-1.0]])]});
            extrude(context, id + "F6", {"entities" : qUnion([Q0, Q1, Q2, Q3, Q4, Q5, Q6, Q7, Q8, Q9, Q10, Q11, Q12, Q13, Q14]), "operationType" : NewBodyOperationType.ADD, "depth" : 1.63 * mm});
        }
    });
